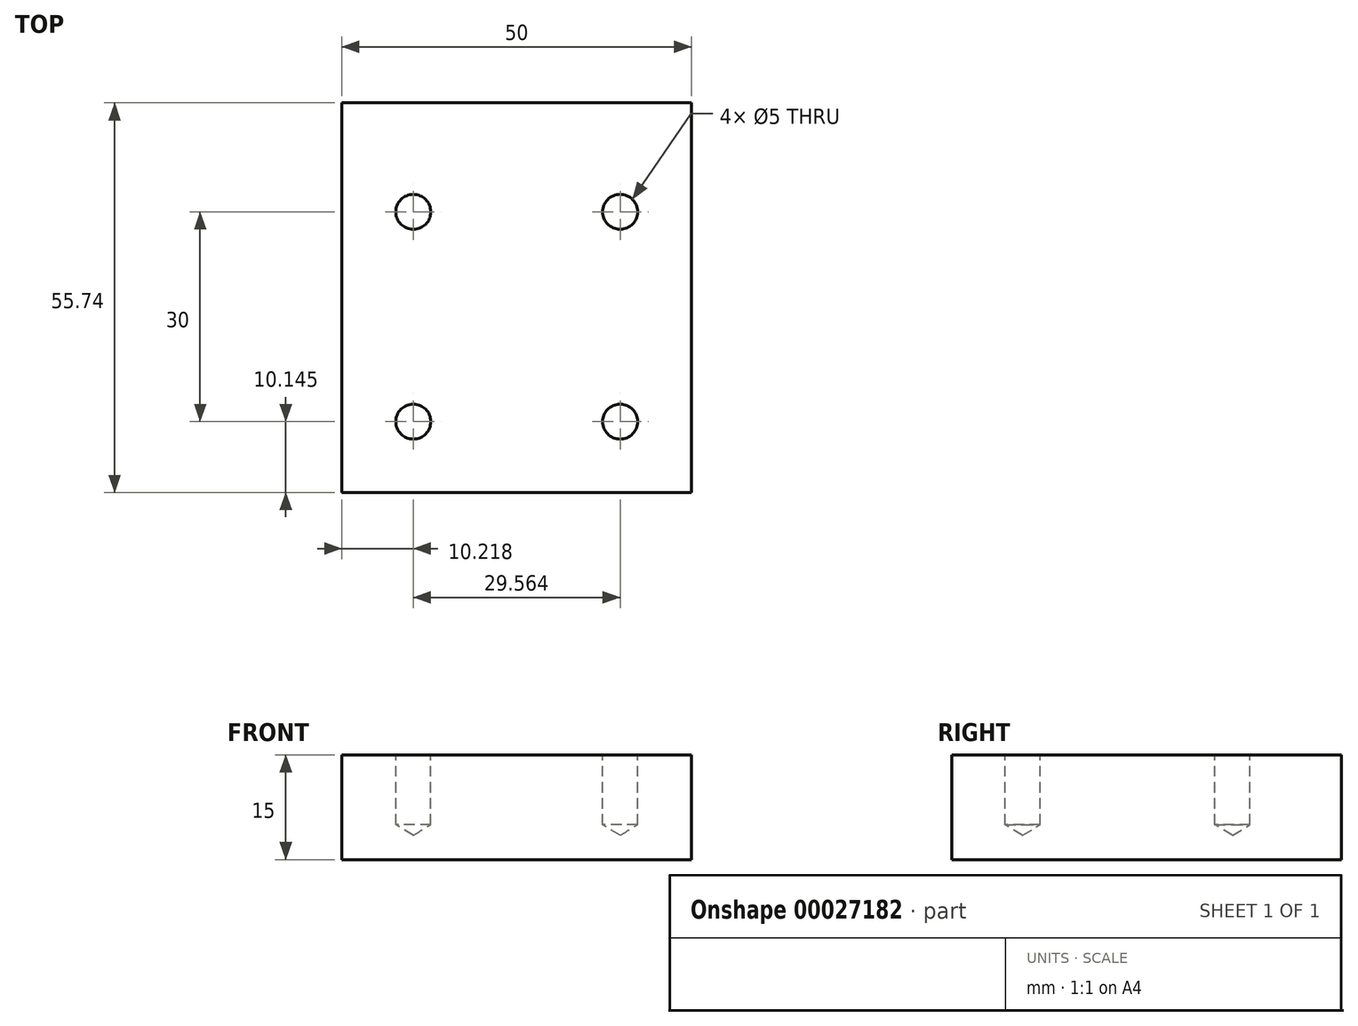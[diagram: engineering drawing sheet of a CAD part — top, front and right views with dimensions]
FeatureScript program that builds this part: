
annotation { "Feature Type Name" : "Feature", "Feature Type Description" : "" }
export const myFeature = defineFeature(function(context is Context, id is Id, definition is map)
    precondition{}
    {
        {
            var Q0;
            Q0=qCreatedBy(makeId("Front.planeOp"),FACE);
            var sketch = newSketch(context, id + "F0", { "sketchPlane" : qUnion([Q0])});
            skLineSegment(sketch, "E0", {"start": v(0, 0) * mm, "end": v(0, 15) * mm});
            skLineSegment(sketch, "E1", {"start": v(0, 15) * mm, "end": v(50, 15) * mm});
            skLineSegment(sketch, "E2", {"start": v(0, 0) * mm, "end": v(50, 0) * mm});
            skLineSegment(sketch, "E3", {"start": v(50, 0) * mm, "end": v(50, 15) * mm});
            skSolve(sketch);
        }
        {
            var Q0;
            Q0=makeQuery(id+"F0.imprint","IMPRINT",FACE,{"disambiguationData":[TD([[makeQuery(id+"F0.imprint","IMPRINT",EDGE,{"derivedFrom":sQuery(id+"F0.wireOp",EDGE,"E0")}),-1.0]])]});
            extrude(context, id + "F1", {"entities" : qUnion([Q0]), "depth" : 55.74 * mm});
        }
        {
            var Q0;
            Q0=makeQuery(id+"F1.opExtrude","SWEPT_FACE",FACE,{"disambiguationData":[OSD([sQuery(id+"F0.wireOp",EDGE,"E1")])]});
            var sketch = newSketch(context, id + "F2", { "sketchPlane" : qUnion([Q0])});
            skLineSegment(sketch, "E4.bottom", {"start": v(10.22, -15.6) * mm, "end": v(39.78, -15.6) * mm, "construction": true});
            skLineSegment(sketch, "E4.top", {"start": v(10.22, -45.6) * mm, "end": v(39.78, -45.6) * mm, "construction": true});
            skLineSegment(sketch, "E4.left", {"start": v(10.22, -15.6) * mm, "end": v(10.22, -45.6) * mm, "construction": true});
            skLineSegment(sketch, "E4.right", {"start": v(39.78, -15.6) * mm, "end": v(39.78, -45.6) * mm, "construction": true});
            skLineSegment(sketch, "E5", {"start": v(10.22, -15.6) * mm, "end": v(25, -30.6) * mm, "construction": true});
            skLineSegment(sketch, "E6", {"start": v(25, -30.6) * mm, "end": v(39.78, -45.6) * mm, "construction": true});
            skLineSegment(sketch, "E7", {"start": v(0, -30.6) * mm, "end": v(50, -30.6) * mm, "construction": true});
            skSolve(sketch);
        }
        {
            var Q0;
            Q0=sQuery(id+"F2.wireOp",VERTEX,"E4.left.start");
            var Q1;
            Q1=sQuery(id+"F2.wireOp",VERTEX,"E4.right.start");
            var Q2;
            Q2=sQuery(id+"F2.wireOp",VERTEX,"E4.left.end");
            var Q3;
            Q3=sQuery(id+"F2.wireOp",VERTEX,"E4.top.end");
            var Q4;
            Q4=makeQuery(id+"F1.opExtrude","SWEPT_BODY",BODY,{"disambiguationData":[OSD([sQuery(id+"F0.wireOp",EDGE,"E0"),sQuery(id+"F0.wireOp",EDGE,"E1"),sQuery(id+"F0.wireOp",EDGE,"E2"),sQuery(id+"F0.wireOp",EDGE,"E3")])]});
            hole(context, id + "F3", {"style" : HoleStyle.SIMPLE, "holeDiameter" : 5 * mm, "endStyle" : HoleEndStyle.BLIND, "holeDepth" : 10 * mm, "locations" : qUnion([Q0, Q1, Q2, Q3]), "scope" : qUnion([Q4])});
        }
    });
